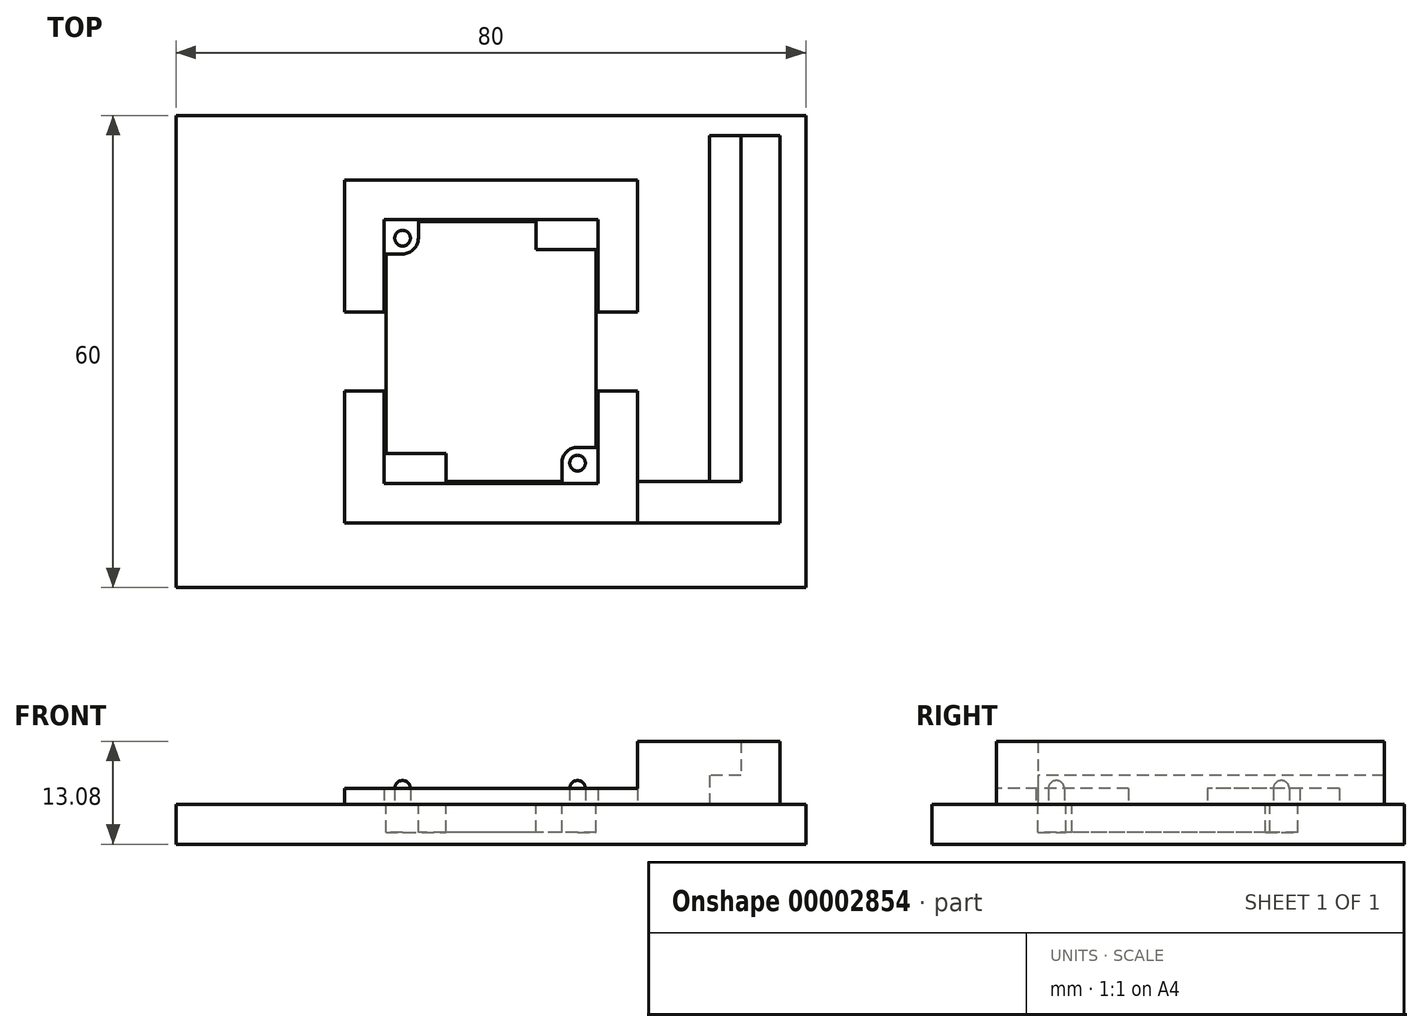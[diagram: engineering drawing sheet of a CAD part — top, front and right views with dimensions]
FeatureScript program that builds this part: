
annotation { "Feature Type Name" : "Feature", "Feature Type Description" : "" }
export const myFeature = defineFeature(function(context is Context, id is Id, definition is map)
    precondition{}
    {
        {
            var Q0;
            Q0=qCreatedBy(makeId("Top.planeOp"),FACE);
            var sketch = newSketch(context, id + "F0", { "sketchPlane" : qUnion([Q0])});
            skLineSegment(sketch, "E0.rect.bottom", {"start": v(13.34, 16.51) * mm, "end": v(-13.33, 16.51) * mm});
            skLineSegment(sketch, "E0.rect.top", {"start": v(13.33, -16.51) * mm, "end": v(-13.34, -16.51) * mm});
            skLineSegment(sketch, "E0.rect.left", {"start": v(13.34, 16.51) * mm, "end": v(13.33, -16.51) * mm});
            skLineSegment(sketch, "E0.rect.right", {"start": v(-13.33, 16.51) * mm, "end": v(-13.34, -16.51) * mm});
            skPoint(sketch, "E0.rect.middle", {"position": v(0, 0) * mm});
            skCircle(sketch, "E1", {"center": v(-11.23, 14.4) * mm, "radius": 1 * mm});
            skCircle(sketch, "E2", {"center": v(11, -14.17) * mm, "radius": 1 * mm});
            skCircle(sketch, "E3", {"center": v(-11.23, 14.4) * mm, "radius": 2 * mm});
            skCircle(sketch, "E4", {"center": v(11, -14.17) * mm, "radius": 2 * mm});
            skLineSegment(sketch, "E5.rect.bottom", {"start": v(-3.6, 4.24) * mm, "end": v(-6.15, 4.24) * mm});
            skLineSegment(sketch, "E5.rect.top", {"start": v(-3.6, -8.46) * mm, "end": v(-6.15, -8.46) * mm});
            skLineSegment(sketch, "E5.rect.left", {"start": v(-3.6, 4.24) * mm, "end": v(-3.6, -8.46) * mm});
            skLineSegment(sketch, "E5.rect.right", {"start": v(-6.15, 4.24) * mm, "end": v(-6.15, -8.46) * mm});
            skPoint(sketch, "E5.rect.middle", {"position": v(-4.88, -2.1) * mm});
            skLineSegment(sketch, "E6", {"start": v(-9.23, 14.4) * mm, "end": v(-9.23, 16.51) * mm});
            skLineSegment(sketch, "E7", {"start": v(-11.23, 12.4) * mm, "end": v(-13.33, 12.4) * mm});
            skLineSegment(sketch, "E8", {"start": v(11, -12.17) * mm, "end": v(13.33, -12.17) * mm});
            skLineSegment(sketch, "E9", {"start": v(9, -14.17) * mm, "end": v(9, -16.51) * mm});
            skLineSegment(sketch, "E10.bottom", {"start": v(-13.34, -16.51) * mm, "end": v(-5.72, -16.51) * mm});
            skLineSegment(sketch, "E10.top", {"start": v(-13.34, -12.95) * mm, "end": v(-5.72, -12.95) * mm});
            skLineSegment(sketch, "E10.left", {"start": v(-13.34, -16.51) * mm, "end": v(-13.34, -12.95) * mm});
            skLineSegment(sketch, "E10.right", {"start": v(-5.72, -16.51) * mm, "end": v(-5.72, -12.95) * mm});
            skLineSegment(sketch, "E11.bottom", {"start": v(13.34, 16.51) * mm, "end": v(5.72, 16.51) * mm});
            skLineSegment(sketch, "E11.top", {"start": v(13.34, 12.95) * mm, "end": v(5.72, 12.95) * mm});
            skLineSegment(sketch, "E11.left", {"start": v(13.34, 16.51) * mm, "end": v(13.34, 12.95) * mm});
            skLineSegment(sketch, "E11.right", {"start": v(5.72, 16.51) * mm, "end": v(5.72, 12.95) * mm});
            skSolve(sketch);
        }
        {
            var Q0;
            Q0=qCreatedBy(makeId("Top.planeOp"),FACE);
            var sketch = newSketch(context, id + "F1", { "sketchPlane" : qUnion([Q0])});
            skLineSegment(sketch, "E12.rect.bottom", {"start": v(40, 30) * mm, "end": v(-40, 30) * mm});
            skLineSegment(sketch, "E12.rect.top", {"start": v(40, -30) * mm, "end": v(-40, -30) * mm});
            skLineSegment(sketch, "E12.rect.left", {"start": v(40, 30) * mm, "end": v(40, -30) * mm});
            skLineSegment(sketch, "E12.rect.right", {"start": v(-40, 30) * mm, "end": v(-40, -30) * mm});
            skPoint(sketch, "E12.rect.middle", {"position": v(0, 0) * mm});
            skSolve(sketch);
        }
        {
            var Q0;
            Q0 = qSketchRegion(id + "F1", true);
            extrude(context, id + "F2", {"entities" : qUnion([Q0]), "oppositeDirection" : true, "depth" : 5.08 * mm});
        }
        {
            var Q0;
            Q0=makeQuery(id+"F0.imprint","IMPRINT",FACE,{"disambiguationData":[TD([[makeQuery(id+"F0.imprint","IMPRINT",EDGE,{"derivedFrom":sQuery(id+"F0.wireOp",EDGE,"E5.rect.bottom")}),-1.0]])]});
            var Q1;
            Q1=makeQuery(id+"F0.imprint","IMPRINT",FACE,{"disambiguationData":[TD([[makeQuery(id+"F0.imprint","IMPRINT",EDGE,{"derivedFrom":sQuery(id+"F0.wireOp",EDGE,"E5.rect.bottom")}),1.0]])]});
            extrude(context, id + "F3", {"entities" : qUnion([Q0, Q1]), "operationType" : NewBodyOperationType.REMOVE, "oppositeDirection" : true, "depth" : 3.56 * mm});
        }
        {
            var Q0;
            Q0=makeQuery(id+"F2.opExtrude","CAP_FACE",FACE,{"disambiguationData":[OSD([sQuery(id+"F1.wireOp",EDGE,"E12.rect.bottom"),sQuery(id+"F1.wireOp",EDGE,"E12.rect.top"),sQuery(id+"F1.wireOp",EDGE,"E12.rect.left"),sQuery(id+"F1.wireOp",EDGE,"E12.rect.right")])],"isStart":true});
            var sketch = newSketch(context, id + "F4", { "sketchPlane" : qUnion([Q0])});
            skCircle(sketch, "E13", {"center": v(-11.23, 14.4) * mm, "radius": 1 * mm});
            skCircle(sketch, "E14", {"center": v(11, -14.17) * mm, "radius": 1 * mm});
            skLineSegment(sketch, "E15", {"start": v(-13.59, 16.76) * mm, "end": v(13.59, 16.76) * mm});
            skLineSegment(sketch, "E16", {"start": v(13.59, 16.76) * mm, "end": v(13.59, -16.76) * mm});
            skLineSegment(sketch, "E17", {"start": v(-13.59, -16.76) * mm, "end": v(13.59, -16.76) * mm});
            skLineSegment(sketch, "E18", {"start": v(-13.59, 16.76) * mm, "end": v(-13.59, -16.76) * mm});
            skLineSegment(sketch, "E19.0", {"start": v(-18.59, 21.76) * mm, "end": v(18.59, 21.76) * mm});
            skLineSegment(sketch, "E19.1", {"start": v(-18.59, 21.76) * mm, "end": v(-18.59, -21.76) * mm});
            skLineSegment(sketch, "E19.2", {"start": v(-18.59, -21.76) * mm, "end": v(18.59, -21.76) * mm});
            skLineSegment(sketch, "E19.3", {"start": v(18.59, 21.76) * mm, "end": v(18.59, -21.76) * mm});
            skLineSegment(sketch, "E20.rect.bottom", {"start": v(18.59, 5) * mm, "end": v(-18.59, 5) * mm});
            skLineSegment(sketch, "E20.rect.top", {"start": v(18.59, -5) * mm, "end": v(-18.59, -5) * mm});
            skLineSegment(sketch, "E20.rect.left", {"start": v(18.59, 5) * mm, "end": v(18.59, -5) * mm});
            skLineSegment(sketch, "E20.rect.right", {"start": v(-18.59, 5) * mm, "end": v(-18.59, -5) * mm});
            skPoint(sketch, "E20.rect.middle", {"position": v(0, 0) * mm});
            skSolve(sketch);
        }
        {
            var Q0;
            {var subQ10=sQuery(id+"F4.wireOp",EDGE,"E15");Q0=makeQuery(id+"F4.imprint","IMPRINT",FACE,{"disambiguationData":[TD([[makeQuery(id+"F4.imprint","IMPRINT",EDGE,{"derivedFrom":subQ10}),1.0]])]});}
            var Q1;
            {var subQ10=sQuery(id+"F4.wireOp",EDGE,"E17");Q1=makeQuery(id+"F4.imprint","IMPRINT",FACE,{"disambiguationData":[TD([[makeQuery(id+"F4.imprint","IMPRINT",EDGE,{"derivedFrom":subQ10}),-1.0]])]});}
            var Q2;
            Q2=makeQuery(id+"F4.imprint","IMPRINT",FACE,{"disambiguationData":[TD([[makeQuery(id+"F4.imprint","IMPRINT",EDGE,{"derivedFrom":sQuery(id+"F4.wireOp",EDGE,"E13")}),1.0]])]});
            var Q3;
            Q3=makeQuery(id+"F4.imprint","IMPRINT",FACE,{"disambiguationData":[TD([[makeQuery(id+"F4.imprint","IMPRINT",EDGE,{"derivedFrom":sQuery(id+"F4.wireOp",EDGE,"E14")}),1.0]])]});
            extrude(context, id + "F5", {"entities" : qUnion([Q0, Q1, Q2, Q3]), "operationType" : NewBodyOperationType.ADD, "depth" : 2 * mm});
        }
        {
            var Q0;
            Q0=makeQuery(id+"F5.opExtrude","CAP_FACE",FACE,{"disambiguationData":[OSD([sQuery(id+"F4.wireOp",EDGE,"E13")])],"isStart":false});
            var sketch = newSketch(context, id + "F6", { "sketchPlane" : qUnion([Q0])});
            skCircle(sketch, "E21", {"center": v(-11.23, 14.4) * mm, "radius": 1 * mm});
            skPoint(sketch, "E21.first.point", {"position": v(-11.79, 15.23) * mm});
            skPoint(sketch, "E21.second.point", {"position": v(-10.27, 14.7) * mm});
            skPoint(sketch, "E21.third.point", {"position": v(-11.68, 13.51) * mm});
            skSolve(sketch);
        }
        {
            var Q0;
            Q0 = qSketchRegion(id + "F6", true);
            extrude(context, id + "F7", {"entities" : qUnion([Q0]), "operationType" : NewBodyOperationType.ADD, "depth" : 1 * mm});
        }
        {
            var Q0;
            Q0=makeQuery(id+"F5.opExtrude","CAP_FACE",FACE,{"disambiguationData":[OSD([sQuery(id+"F4.wireOp",EDGE,"E14")])],"isStart":false});
            var sketch = newSketch(context, id + "F8", { "sketchPlane" : qUnion([Q0])});
            skCircle(sketch, "E22", {"center": v(11, -14.17) * mm, "radius": 1 * mm});
            skPoint(sketch, "E22.first.point", {"position": v(10.28, -13.48) * mm});
            skPoint(sketch, "E22.second.point", {"position": v(11.83, -13.62) * mm});
            skPoint(sketch, "E22.third.point", {"position": v(10.7, -15.13) * mm});
            skSolve(sketch);
        }
        {
            var Q0;
            Q0 = qSketchRegion(id + "F8", true);
            extrude(context, id + "F9", {"entities" : qUnion([Q0]), "operationType" : NewBodyOperationType.ADD, "depth" : 1 * mm});
        }
        {
            var Q0;
            Q0=makeQuery(id+"F9.opExtrude","CAP_EDGE",EDGE,{"disambiguationData":[OSD([sQuery(id+"F8.wireOp",EDGE,"E22")])],"isStart":false});
            var Q1;
            Q1=makeQuery(id+"F7.opExtrude","CAP_EDGE",EDGE,{"disambiguationData":[OSD([sQuery(id+"F6.wireOp",EDGE,"E21")])],"isStart":false});
            fillet(context, id + "F10", {"entities" : qUnion([Q0, Q1]), "radius" : 1 * mm, "tangentPropagation" : true, "allowEdgeOverflow" : false});
        }
        {
            var Q0;
            Q0=makeQuery(id+"F2.opExtrude","CAP_FACE",FACE,{"disambiguationData":[OSD([sQuery(id+"F1.wireOp",EDGE,"E12.rect.bottom"),sQuery(id+"F1.wireOp",EDGE,"E12.rect.top"),sQuery(id+"F1.wireOp",EDGE,"E12.rect.left"),sQuery(id+"F1.wireOp",EDGE,"E12.rect.right")])],"isStart":true});
            var sketch = newSketch(context, id + "F11", { "sketchPlane" : qUnion([Q0])});
            skLineSegment(sketch, "E23.rect.bottom", {"start": v(31.73, 27.46) * mm, "end": v(-7.42, 27.46) * mm});
            skLineSegment(sketch, "E23.rect.top", {"start": v(31.73, -16.54) * mm, "end": v(-7.42, -16.54) * mm});
            skLineSegment(sketch, "E23.rect.left", {"start": v(31.73, 27.46) * mm, "end": v(31.73, -16.54) * mm});
            skLineSegment(sketch, "E23.rect.right", {"start": v(-7.42, 27.46) * mm, "end": v(-7.42, -16.54) * mm});
            skPoint(sketch, "E23.rect.middle", {"position": v(12.15, 5.46) * mm});
            skLineSegment(sketch, "E24.rect.bottom", {"start": v(-3.86, -5.01) * mm, "end": v(-5.9, -5.01) * mm});
            skLineSegment(sketch, "E24.rect.top", {"start": v(-3.86, 9.23) * mm, "end": v(-5.9, 9.23) * mm});
            skLineSegment(sketch, "E24.rect.left", {"start": v(-3.86, -5.01) * mm, "end": v(-3.86, 9.23) * mm});
            skLineSegment(sketch, "E24.rect.right", {"start": v(-5.9, -5.01) * mm, "end": v(-5.9, 9.23) * mm});
            skPoint(sketch, "E24.rect.middle", {"position": v(-4.88, 2.1) * mm});
            skLineSegment(sketch, "E25", {"start": v(18.59, -21.76) * mm, "end": v(36.73, -21.76) * mm});
            skLineSegment(sketch, "E26", {"start": v(36.73, 27.46) * mm, "end": v(36.73, -21.76) * mm});
            skLineSegment(sketch, "E27", {"start": v(31.73, 27.46) * mm, "end": v(36.73, 27.46) * mm});
            skSolve(sketch);
        }
        {
            var Q0;
            {var subQ6=sQuery(id+"F11.wireOp",EDGE,"E23.rect.left");Q0=makeQuery(id+"F11.imprint","IMPRINT",FACE,{"disambiguationData":[TD([[makeQuery(id+"F11.imprint","IMPRINT",EDGE,{"derivedFrom":subQ6}),1.0]])]});}
            extrude(context, id + "F12", {"entities" : qUnion([Q0]), "operationType" : NewBodyOperationType.ADD, "depth" : 8 * mm});
        }
        {
            var Q0;
            Q0=makeQuery(id+"F2.opExtrude","CAP_FACE",FACE,{"disambiguationData":[OSD([sQuery(id+"F1.wireOp",EDGE,"E12.rect.bottom"),sQuery(id+"F1.wireOp",EDGE,"E12.rect.top"),sQuery(id+"F1.wireOp",EDGE,"E12.rect.left"),sQuery(id+"F1.wireOp",EDGE,"E12.rect.right")])],"isStart":true});
            var sketch = newSketch(context, id + "F13", { "sketchPlane" : qUnion([Q0])});
            skLineSegment(sketch, "E28.bottom", {"start": v(31.73, 27.46) * mm, "end": v(27.73, 27.46) * mm});
            skLineSegment(sketch, "E28.top", {"start": v(31.73, -16.54) * mm, "end": v(27.73, -16.54) * mm});
            skLineSegment(sketch, "E28.left", {"start": v(31.73, 27.46) * mm, "end": v(31.73, -16.54) * mm});
            skLineSegment(sketch, "E28.right", {"start": v(27.73, 27.46) * mm, "end": v(27.73, -16.54) * mm});
            skSolve(sketch);
        }
        {
            var Q0;
            Q0 = qSketchRegion(id + "F13", true);
            extrude(context, id + "F14", {"entities" : qUnion([Q0]), "operationType" : NewBodyOperationType.ADD, "depth" : 3.65 * mm});
        }
    });
